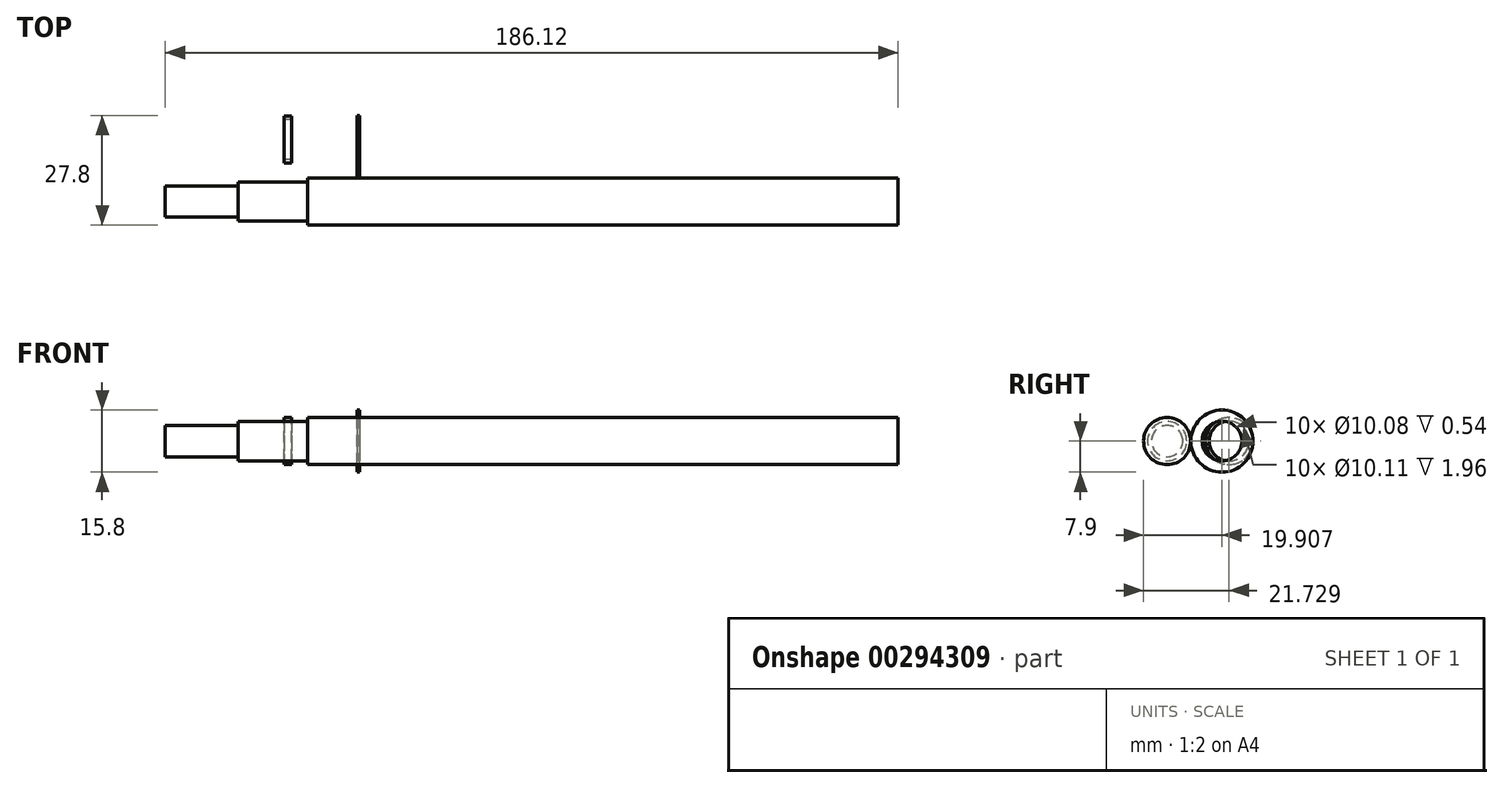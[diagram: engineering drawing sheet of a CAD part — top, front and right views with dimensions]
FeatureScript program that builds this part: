
annotation { "Feature Type Name" : "Feature", "Feature Type Description" : "" }
export const myFeature = defineFeature(function(context is Context, id is Id, definition is map)
    precondition{}
    {
        {
            var Q0;
            Q0=qCreatedBy(makeId("Top.planeOp"),FACE);
            var sketch = newSketch(context, id + "F0", { "sketchPlane" : qUnion([Q0])});
            skLineSegment(sketch, "E0", {"start": v(-28.65, 0) * mm, "end": v(-28.65, 3.98) * mm});
            skLineSegment(sketch, "E1", {"start": v(-28.65, 3.98) * mm, "end": v(-10.13, 3.98) * mm});
            skLineSegment(sketch, "E2", {"start": v(-10.13, 3.98) * mm, "end": v(-10.13, 4.98) * mm});
            skLineSegment(sketch, "E3", {"start": v(-10.13, 4.98) * mm, "end": v(7.47, 4.98) * mm});
            skLineSegment(sketch, "E4", {"start": v(7.47, 4.98) * mm, "end": v(7.47, 5.98) * mm});
            skLineSegment(sketch, "E5", {"start": v(7.47, 5.98) * mm, "end": v(157.47, 5.98) * mm});
            skLineSegment(sketch, "E6", {"start": v(157.47, 5.98) * mm, "end": v(157.47, 0) * mm});
            skLineSegment(sketch, "E7", {"start": v(157.47, 0) * mm, "end": v(-28.65, 0) * mm});
            skSolve(sketch);
        }
        {
            var Q0;
            Q0 = qSketchRegion(id + "F0", true);
            var Q1;
            Q1=sQuery(id+"F0.wireOp",EDGE,"E7");
            revolve(context, id + "F1", {"entities" : qUnion([Q0]), "axis" : qUnion([Q1]), "revolveType" : RevolveType.FULL});
        }
        {
            var Q0;
            Q0=qCreatedBy(makeId("Top.planeOp"),FACE);
            var sketch = newSketch(context, id + "F2", { "sketchPlane" : qUnion([Q0])});
            skLineSegment(sketch, "E8", {"start": v(-4.79, 15.75) * mm, "end": v(10.96, 15.75) * mm, "construction": true});
            skLineSegment(sketch, "E9.bottom", {"start": v(1.5, 21.73) * mm, "end": v(3.45, 21.73) * mm});
            skLineSegment(sketch, "E9.top", {"start": v(1.5, 20.8) * mm, "end": v(3.45, 20.8) * mm});
            skLineSegment(sketch, "E9.left", {"start": v(1.5, 21.73) * mm, "end": v(1.5, 20.8) * mm});
            skLineSegment(sketch, "E9.right", {"start": v(3.45, 21.73) * mm, "end": v(3.45, 20.8) * mm});
            skSolve(sketch);
        }
        {
            var Q0;
            Q0 = qSketchRegion(id + "F2", true);
            var Q1;
            Q1=sQuery(id+"F2.wireOp",EDGE,"E8");
            revolve(context, id + "F3", {"entities" : qUnion([Q0]), "axis" : qUnion([Q1]), "revolveType" : RevolveType.FULL});
        }
        {
            var Q0;
            Q0=qCreatedBy(makeId("Top.planeOp"),FACE);
            var sketch = newSketch(context, id + "F4", { "sketchPlane" : qUnion([Q0])});
            skLineSegment(sketch, "E10", {"start": v(15.44, 13.93) * mm, "end": v(33.16, 13.93) * mm, "construction": true});
            skLineSegment(sketch, "E11.bottom", {"start": v(20.09, 21.82) * mm, "end": v(20.63, 21.82) * mm});
            skLineSegment(sketch, "E11.top", {"start": v(20.09, 18.97) * mm, "end": v(20.63, 18.97) * mm});
            skLineSegment(sketch, "E11.left", {"start": v(20.09, 21.82) * mm, "end": v(20.09, 18.97) * mm});
            skLineSegment(sketch, "E11.right", {"start": v(20.63, 21.82) * mm, "end": v(20.63, 18.97) * mm});
            skSolve(sketch);
        }
        {
            var Q0;
            Q0 = qSketchRegion(id + "F4", true);
            var Q1;
            Q1=sQuery(id+"F4.wireOp",EDGE,"E10");
            revolve(context, id + "F5", {"entities" : qUnion([Q0]), "axis" : qUnion([Q1]), "revolveType" : RevolveType.FULL});
        }
    });
